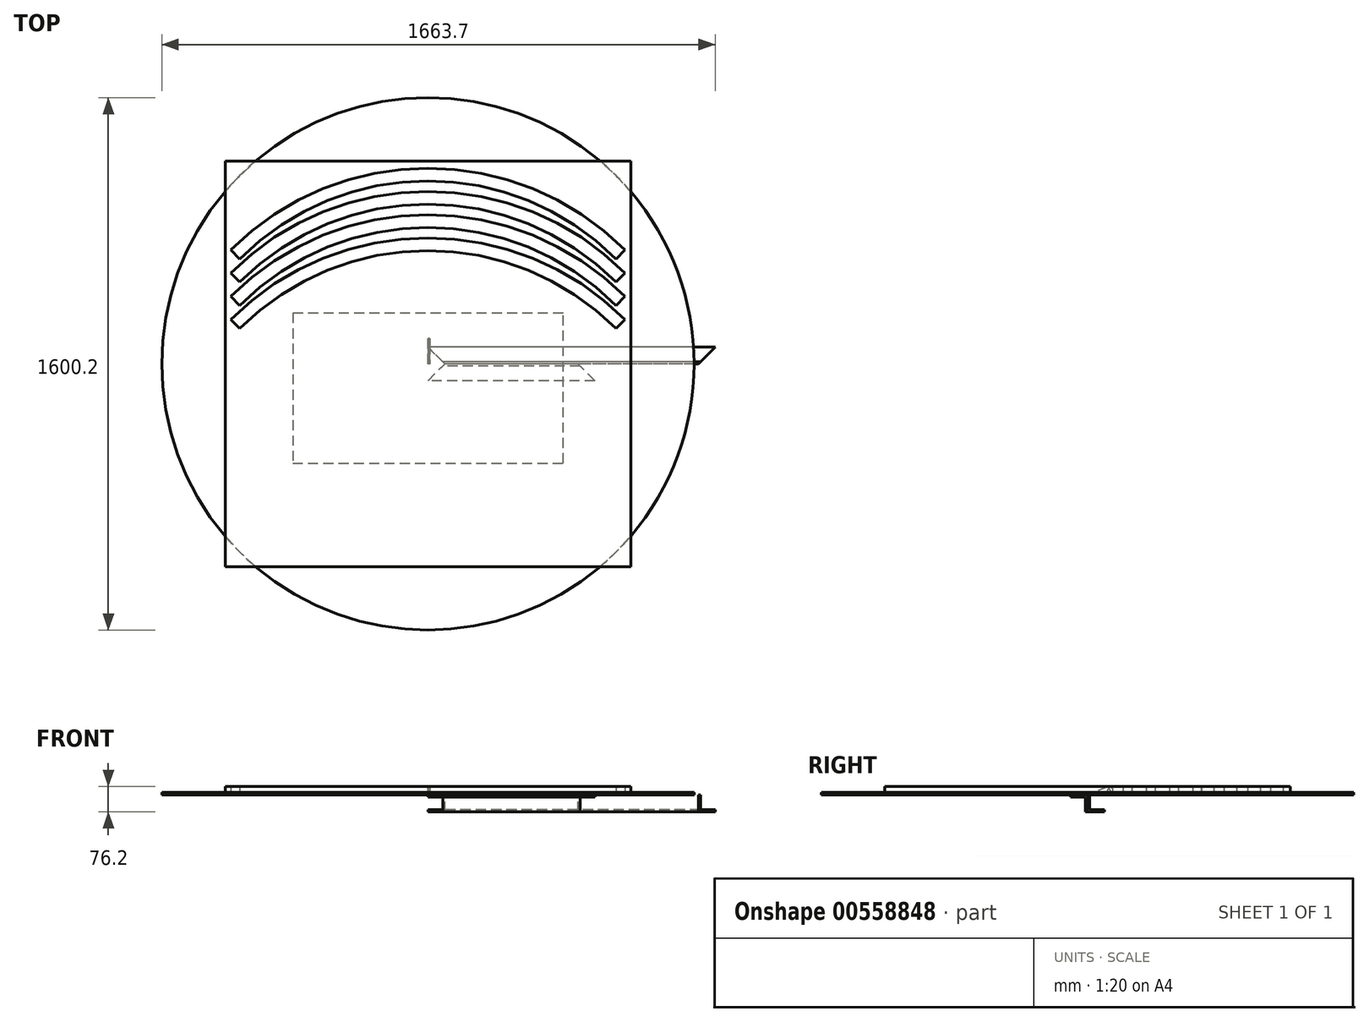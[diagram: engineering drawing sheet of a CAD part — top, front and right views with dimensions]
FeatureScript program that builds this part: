
annotation { "Feature Type Name" : "Feature", "Feature Type Description" : "" }
export const myFeature = defineFeature(function(context is Context, id is Id, definition is map)
    precondition{}
    {
        {
            var Q0;
            Q0=qCreatedBy(makeId("Top.planeOp"),FACE);
            var sketch = newSketch(context, id + "F0", { "sketchPlane" : qUnion([Q0])});
            skCircle(sketch, "E0", {"center": v(0, 0) * mm, "radius": 800.1 * mm});
            skLineSegment(sketch, "E1", {"start": v(0, 152.4) * mm, "end": v(-406.4, 152.4) * mm});
            skLineSegment(sketch, "E2", {"start": v(-406.4, 152.4) * mm, "end": v(-406.4, -298.45) * mm});
            skLineSegment(sketch, "E3", {"start": v(-406.4, -298.45) * mm, "end": v(406.4, -298.45) * mm});
            skLineSegment(sketch, "E4", {"start": v(406.4, -298.45) * mm, "end": v(406.4, 152.4) * mm});
            skLineSegment(sketch, "E5", {"start": v(406.4, 152.4) * mm, "end": v(0, 152.4) * mm});
            skSolve(sketch);
        }
        {
            var Q0;
            Q0=makeQuery(id+"F0.imprint","IMPRINT",FACE,{"disambiguationData":[TD([[makeQuery(id+"F0.imprint","IMPRINT",EDGE,{"derivedFrom":sQuery(id+"F0.wireOp",EDGE,"E0")}),1.0]])]});
            extrude(context, id + "F1", {"entities" : qUnion([Q0]), "depth" : 7.94 * mm, "offsetDistance" : 25.4 * mm});
        }
        {
            var Q0;
            Q0=qCreatedBy(makeId("Right.planeOp"),FACE);
            var sketch = newSketch(context, id + "F2", { "sketchPlane" : qUnion([Q0])});
            skLineSegment(sketch, "E6", {"start": v(0, 0) * mm, "end": v(76.2, 0) * mm});
            skLineSegment(sketch, "E7", {"start": v(76.2, 0) * mm, "end": v(76.2, 12.7) * mm});
            skLineSegment(sketch, "E8", {"start": v(58.62, 24.42) * mm, "end": v(0, 0) * mm});
            skPoint(sketch, "E9.visualSharp", {"position": v(76.2, 31.75) * mm});
            skArc(sketch, "E9.filletArc", {"start": v(76.2, 12.7) * mm, "mid": v(70.54, 23.27) * mm, "end": v(58.62, 24.42) * mm});
            skCircle(sketch, "E10", {"center": v(63.5, 12.7) * mm, "radius": 4.76 * mm});
            skSolve(sketch);
        }
        {
            var Q0;
            Q0 = qSketchRegion(id + "F2", true);
            extrude(context, id + "F3", {"entities" : qUnion([Q0]), "depth" : 6.35 * mm, "offsetDistance" : 25.4 * mm});
        }
        {
            var Q0;
            Q0=qCreatedBy(makeId("Top.planeOp"),FACE);
            var sketch = newSketch(context, id + "F4", { "sketchPlane" : qUnion([Q0])});
            skLineSegment(sketch, "E11.0", {"start": v(-406.4, 152.4) * mm, "end": v(-406.4, -298.45) * mm});
            skLineSegment(sketch, "E12.0", {"start": v(-406.4, -298.45) * mm, "end": v(406.4, -298.45) * mm});
            skLineSegment(sketch, "E13.0", {"start": v(406.4, 152.4) * mm, "end": v(-406.4, 152.4) * mm});
            skLineSegment(sketch, "E14.0", {"start": v(406.4, -298.45) * mm, "end": v(406.4, 152.4) * mm});
            skSolve(sketch);
        }
        {
            var Q0;
            Q0 = qSketchRegion(id + "F4", true);
            extrude(context, id + "F5", {"entities" : qUnion([Q0]), "depth" : 7.94 * mm, "offsetDistance" : 25.4 * mm});
        }
        {
            var Q0;
            Q0=qCreatedBy(makeId("Right.planeOp"),FACE);
            var sketch = newSketch(context, id + "F6", { "sketchPlane" : qUnion([Q0])});
            skLineSegment(sketch, "E15", {"start": v(0, 0) * mm, "end": v(0, -50.8) * mm});
            skLineSegment(sketch, "E16", {"start": v(0, -50.8) * mm, "end": v(50.8, -50.8) * mm});
            skLineSegment(sketch, "E17", {"start": v(50.8, -50.8) * mm, "end": v(50.8, -44.45) * mm});
            skLineSegment(sketch, "E18", {"start": v(50.8, -44.45) * mm, "end": v(6.35, -44.45) * mm});
            skLineSegment(sketch, "E19", {"start": v(6.35, -44.45) * mm, "end": v(6.35, 0) * mm});
            skLineSegment(sketch, "E20", {"start": v(6.35, 0) * mm, "end": v(0, 0) * mm});
            skSolve(sketch);
        }
        {
            var Q0;
            Q0=makeQuery(id+"F6.imprint","IMPRINT",FACE,{"disambiguationData":[TD([[makeQuery(id+"F6.imprint","IMPRINT",EDGE,{"derivedFrom":sQuery(id+"F6.wireOp",EDGE,"E15")}),1.0]])]});
            extrude(context, id + "F7", {"entities" : qUnion([Q0]), "depth" : 863.6 * mm, "offsetDistance" : 25.4 * mm});
        }
        {
            var Q0;
            Q0=qCreatedBy(makeId("Top.planeOp"),FACE);
            var sketch = newSketch(context, id + "F8", { "sketchPlane" : qUnion([Q0])});
            skLineSegment(sketch, "E21.0.0", {"start": v(0, 0) * mm, "end": v(0, 50.8) * mm});
            skLineSegment(sketch, "E21.0.2", {"start": v(863.6, 50.8) * mm, "end": v(863.6, 0) * mm});
            skLineSegment(sketch, "E22", {"start": v(0, 50.8) * mm, "end": v(50.8, 0) * mm});
            skLineSegment(sketch, "E23", {"start": v(863.6, 50.8) * mm, "end": v(812.8, 0) * mm});
            skLineSegment(sketch, "E24", {"start": v(863.6, 0) * mm, "end": v(812.8, 0) * mm});
            skLineSegment(sketch, "E25", {"start": v(0, 0) * mm, "end": v(50.8, 0) * mm});
            skSolve(sketch);
        }
        {
            var Q0;
            Q0 = qSketchRegion(id + "F8", true);
            extrude(context, id + "F9", {"entities" : qUnion([Q0]), "operationType" : NewBodyOperationType.REMOVE, "oppositeDirection" : true, "depth" : 50.8 * mm, "offsetDistance" : 25.4 * mm});
        }
        {
            var Q0;
            Q0=qCreatedBy(makeId("Right.planeOp"),FACE);
            var sketch = newSketch(context, id + "F10", { "sketchPlane" : qUnion([Q0])});
            skLineSegment(sketch, "E26", {"start": v(0, 0) * mm, "end": v(-50.8, 0) * mm});
            skLineSegment(sketch, "E27", {"start": v(-50.8, 0) * mm, "end": v(-50.8, -6.35) * mm});
            skLineSegment(sketch, "E28", {"start": v(-50.8, -6.35) * mm, "end": v(-6.35, -6.35) * mm});
            skLineSegment(sketch, "E29", {"start": v(-6.35, -6.35) * mm, "end": v(-6.35, -50.8) * mm});
            skLineSegment(sketch, "E30", {"start": v(-6.35, -50.8) * mm, "end": v(0, -50.8) * mm});
            skLineSegment(sketch, "E31", {"start": v(0, -50.8) * mm, "end": v(0, 0) * mm});
            skSolve(sketch);
        }
        {
            var Q0;
            Q0 = qSketchRegion(id + "F10", true);
            extrude(context, id + "F11", {"entities" : qUnion([Q0]), "depth" : 501.65 * mm, "offsetDistance" : 25.4 * mm});
        }
        {
            var Q0;
            Q0=qCreatedBy(makeId("Top.planeOp"),FACE);
            var sketch = newSketch(context, id + "F12", { "sketchPlane" : qUnion([Q0])});
            skPoint(sketch, "E32.0", {"position": v(0, -25.4) * mm});
            skLineSegment(sketch, "E33.0", {"start": v(501.65, 0) * mm, "end": v(501.65, -50.8) * mm});
            skLineSegment(sketch, "E34", {"start": v(0, -50.8) * mm, "end": v(50.8, 0) * mm});
            skLineSegment(sketch, "E35", {"start": v(501.65, -50.8) * mm, "end": v(450.85, 0) * mm});
            skLineSegment(sketch, "E36", {"start": v(0, 0) * mm, "end": v(50.8, 0) * mm});
            skLineSegment(sketch, "E37", {"start": v(450.85, 0) * mm, "end": v(501.65, 0) * mm});
            skLineSegment(sketch, "E38.0", {"start": v(0, 0) * mm, "end": v(0, -50.8) * mm});
            skSolve(sketch);
        }
        {
            var Q0;
            Q0 = qSketchRegion(id + "F12", true);
            extrude(context, id + "F13", {"entities" : qUnion([Q0]), "operationType" : NewBodyOperationType.REMOVE, "oppositeDirection" : true, "depth" : 50.8 * mm, "offsetDistance" : 25.4 * mm});
        }
        {
            var Q0;
            Q0=qCreatedBy(makeId("Top.planeOp"),FACE);
            var sketch = newSketch(context, id + "F14", { "sketchPlane" : qUnion([Q0])});
            skLineSegment(sketch, "E39.bottom", {"start": v(609.6, -609.6) * mm, "end": v(-609.6, -609.6) * mm});
            skLineSegment(sketch, "E39.top", {"start": v(609.6, 609.6) * mm, "end": v(-609.6, 609.6) * mm});
            skLineSegment(sketch, "E39.left", {"start": v(609.6, -609.6) * mm, "end": v(609.6, 609.6) * mm});
            skLineSegment(sketch, "E39.right", {"start": v(-609.6, -609.6) * mm, "end": v(-609.6, 609.6) * mm});
            skPoint(sketch, "E39.middle", {"position": v(0, 0) * mm});
            skArc(sketch, "E40", {"start": v(592.7, 342.34) * mm, "mid": v(0, 587.84) * mm, "end": v(-592.7, 342.34) * mm});
            skArc(sketch, "E41", {"start": v(565.76, 315.4) * mm, "mid": v(0, 549.74) * mm, "end": v(-565.76, 315.4) * mm});
            skLineSegment(sketch, "E42", {"start": v(565.76, 315.4) * mm, "end": v(592.7, 342.34) * mm});
            skLineSegment(sketch, "E43", {"start": v(-565.76, 315.4) * mm, "end": v(-592.7, 342.34) * mm});
            skArc(sketch, "E44", {"start": v(592.7, 272.83) * mm, "mid": v(0, 518.34) * mm, "end": v(-592.7, 272.83) * mm});
            skArc(sketch, "E45", {"start": v(565.76, 245.9) * mm, "mid": v(0, 480.24) * mm, "end": v(-565.76, 245.9) * mm});
            skLineSegment(sketch, "E46", {"start": v(565.76, 245.9) * mm, "end": v(592.7, 272.83) * mm});
            skLineSegment(sketch, "E47", {"start": v(-565.76, 245.9) * mm, "end": v(-592.7, 272.83) * mm});
            skArc(sketch, "E48", {"start": v(592.7, 202.61) * mm, "mid": v(0, 448.11) * mm, "end": v(-592.7, 202.61) * mm});
            skArc(sketch, "E49", {"start": v(565.76, 175.67) * mm, "mid": v(0, 410.01) * mm, "end": v(-565.76, 175.67) * mm});
            skLineSegment(sketch, "E50", {"start": v(565.76, 175.67) * mm, "end": v(592.7, 202.61) * mm});
            skLineSegment(sketch, "E51", {"start": v(-565.76, 175.67) * mm, "end": v(-592.7, 202.61) * mm});
            skArc(sketch, "E52", {"start": v(592.7, 133.1) * mm, "mid": v(0, 378.6) * mm, "end": v(-592.7, 133.1) * mm});
            skArc(sketch, "E53", {"start": v(565.76, 106.16) * mm, "mid": v(0, 340.5) * mm, "end": v(-565.76, 106.16) * mm});
            skLineSegment(sketch, "E54", {"start": v(565.76, 106.16) * mm, "end": v(592.7, 133.1) * mm});
            skLineSegment(sketch, "E55", {"start": v(-565.76, 106.16) * mm, "end": v(-592.7, 133.1) * mm});
            skSolve(sketch);
        }
        {
            var Q0;
            Q0 = qSketchRegion(id + "F14", true);
            extrude(context, id + "F15", {"entities" : qUnion([Q0]), "depth" : 25.4 * mm, "offsetDistance" : 25.4 * mm});
        }
    });
